# Revit family: VL2S-GFS150xWSxBQPx
name_source: partatom
category: Leuchten
units: mm (PartAtom-declared; Revit-internal decimal feet)

## family parameters
Basisbauteil = Fläche
Beim Laden mit Abzugskörper schneiden = Nein
Bemaßung runder Anschluss = Durchmesser verwenden
Gemeinsam genutzt = Nein
Lichtquelle = Ja
OmniClass-Nummer = 23.80.70.11
OmniClass-Titel = Luminaries for Internal Lighting
Raumberechnungspunkt = Nein
Teiletyp = Normal

## types (16) — shared parameters
Baugruppenkennzeichen = D5020200
Datei für fotometrisches Netz = VL2S-GFS_BQP.IES
Emissionsform beim Rendern sichtbar = Nein
Farbfilter = 16777215
Farbtemperaturverschiebung bei Dämpfen der Lampe = <Keine Auswahl>
Hersteller = RIDI Leuchten GmbH
Lampe = LED
Neigungswinkel = 90.00°
URL = www.ridi.de
Von Breite des Rechtecks ausssenden = 1477 mm  [stored 4.8458 ft]
Von Länge des Rechtecks aussenden = 85 mm  [stored 0.278871 ft]
brand = RIDI
conformity mark = CE
electrical safety class = 1
height = 77 mm  [stored 0.252625 ft]
ingress protection (IP) code = IP54
length = 1500 mm  [stored 4.92126 ft]
nominal frequency = 50-60Hz
nominal voltage = 230
voltage type (AC, DC, UC) = AC
width = 97 mm  [stored 0.318241 ft]
zero-valued in all types: Vorgabe-Ansicht

## per-type parameters (varying)
| type | Modell | Scheinlast | rated input power | weight |
| VL2S-GFS150-5FLWS840BQP0750 | 2550140 | 53 VA | 53 | 3,1 kg |
| VL2S-GFS150-5FLWS840BQP1500 | 2550143 | 103 VA | 103 | 3,5 kg |
| VL2S-GFS150-5FLWS830BQP0700 | 2550149 | 53 VA | 53 | 2,9 kg |
| VL2S-GFS150-5FLWS830BQP1500 | 2550152 | 103 VA | 103 | 3,3 kg |
| VL2S-GFS150-5FLWS850BQP0750 | 2550155 | 53 VA | 53 | 2,9 kg |
| VL2S-GFS150-5FLWS850BQP1500 | 2550158 | 103 VA | 103 | 3,3 kg |
| VL2S-GFS150-5FLWS865BQP0700 | 2550161 | 53 VA | 53 | 2,9 kg |
| VL2S-GFS150-5FLWS865BQP1500 | 2550164 | 103 VA | 103 | 3,3 kg |
| VL2S-GFS150-7DAWS840BQP0750 | 2560140 | 52 VA | 52 | 3,1 kg |
| VL2S-GFS150-7DAWS840BQP1500 | 2560143 | 102 VA | 102 | 3,5 kg |
| VL2S-GFS150-7DAWS830BQP0700 | 2560149 | 52 VA | 52 | 2,9 kg |
| VL2S-GFS150-7DAWS830BQP1500 | 2560152 | 102 VA | 102 | 2,9 kg |
| VL2S-GFS150-7DAWS850BQP0750 | 2560155 | 52 VA | 52 | 2,9 kg |
| VL2S-GFS150-7DAWS850BQP1500 | 2560158 | 102 VA | 102 | 3,3 kg |
| VL2S-GFS150-7DAWS865BQP0700 | 2560161 | 52 VA | 52 | 2,9 kg |
| VL2S-GFS150-7DAWS865BQP1500 | 2560164 | 102 VA | 102 | 3,3 kg |

note: column(s) folded — value = type name in every type: product name

note: [stored X ft] marks values corroborated as IEEE doubles in the binary element streams (Revit-internal decimal feet)
